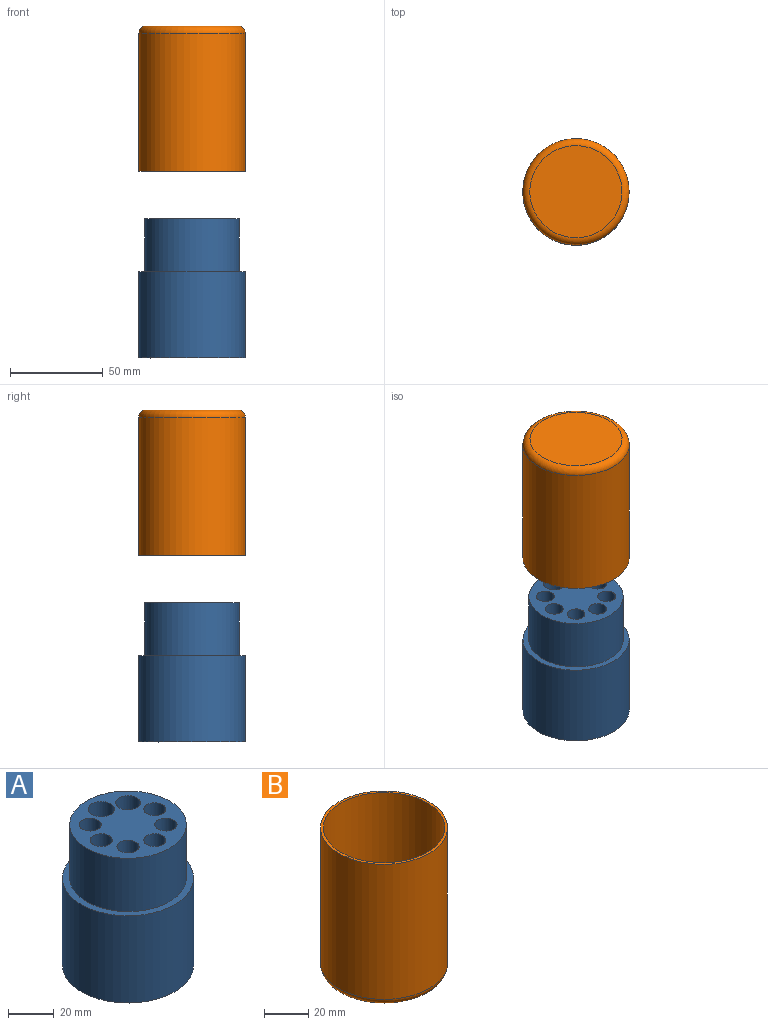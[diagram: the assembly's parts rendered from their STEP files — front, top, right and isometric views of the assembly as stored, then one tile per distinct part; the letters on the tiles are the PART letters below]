
ASSEMBLY  parts=2 mates=1
PART A: 21 faces, bbox 57.2x57.2x74.9 mm
  f0: cylinder r=28.57mm len=57.15mm, axis (0,0,-1), area 8345.5mm2, adj f1,f2
  f1: plane 57.15x57.15mm, normal (0,0,1), area 538.4mm2, adj f0,f3
  f2: plane 57.15x57.15mm, normal (0,0,-1), area 2565.2mm2, adj f0
  f3: cylinder r=25.4mm len=50.8mm, axis (0,0,-1), area 4540.1mm2, adj f1,f4
  f4: plane 50.8x50.8mm, normal (0,0,1), area 1395.8mm2, adj f3,f5,f7,f9,f11,f13,f15,f17
  f5: cylinder r=5.71mm len=67.31mm, axis (0,0,1), area 2417mm2, adj f4,f6
  f6: plane 11.43x11.43mm, normal (0,0,1), area 102.6mm2, adj f5
  f7: cylinder r=5.33mm len=67.31mm, axis (0,0,1), area 2255.9mm2, adj f4,f8
  f8: plane 10.67x10.67mm, normal (0,0,1), area 89.4mm2, adj f7
  f9: cylinder r=4.83mm len=67.31mm, axis (0,0,1), area 2041mm2, adj f4,f10
  f10: plane 9.65x9.65mm, normal (0,0,1), area 73.2mm2, adj f9
  f11: cylinder r=4.83mm len=67.31mm, axis (0,0,1), area 2041mm2, adj f4,f12
  f12: plane 9.65x9.65mm, normal (0,0,1), area 73.2mm2, adj f11
  f13: cylinder r=4.83mm len=67.31mm, axis (0,0,1), area 2041mm2, adj f4,f14
  f14: plane 9.65x9.65mm, normal (0,0,1), area 73.2mm2, adj f13
  f15: cylinder r=4.83mm len=67.31mm, axis (0,0,1), area 2041mm2, adj f4,f16
  f16: plane 9.65x9.65mm, normal (0,0,1), area 73.2mm2, adj f15
  f17: cylinder r=4.83mm len=67.31mm, axis (0,0,1), area 2041mm2, adj f4,f18
  f18: plane 9.65x9.65mm, normal (0,0,1), area 73.2mm2, adj f17
  f19: cylinder r=4.83mm len=67.31mm, axis (0,0,1), area 2041mm2, adj f4,f20
  f20: plane 9.65x9.65mm, normal (0,0,1), area 73.2mm2, adj f19
PART B: 6 faces, bbox 61.9x61.9x78.2 mm
  f0: cylinder r=27.3mm len=66.42mm, axis (0,0,-1), area 11395.3mm2, adj f2,f4
  f1: cylinder r=28.57mm len=74.42mm, axis (0,0,-1), area 13361.9mm2, adj f2,f5
  f2: plane 57.15x57.15mm, normal (0,0,1), area 223mm2, adj f0,f1
  f3: plane 49.53x49.53mm, normal (0,0,-1), area 1926.8mm2, adj f5
  f4: plane 54.61x54.61mm, normal (0,0,1), area 2342.3mm2, adj f0
  f5: torus R=24.77mm, axis (0,0,1), area 1022.5mm2, adj f1,f3
PLACE A rot(axis=(-0.33,-0.45,-0.83),0deg) t=(27.4,30.14,43.9)mm fixed
PLACE B rot(axis=(1,0,0),180deg) t=(27.4,30.14,222.46)mm
MATE slider B.f0 <-> A.f3  axis (0,0,1) through (27.4,30.14,144.23)mm
